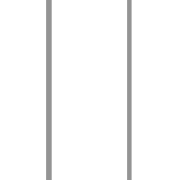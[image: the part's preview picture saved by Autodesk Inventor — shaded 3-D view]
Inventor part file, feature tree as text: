
AUTODESK INVENTOR PART (.ipt)
format: ipt  version: 2021 (Build 250183000, 183)  size: 129,536 bytes
history: native  units: in
note: dims shown in document units (in); Inventor stores cm internally (conversion verified against a paired STEP export)
features: other x4, sketch x4, plane x2, hole x1
ambient origin geometry x8: Origin, YZ Plane, XZ Plane, XY Plane, X Axis, Y Axis, Z Axis, Center Point
bodies: Solid1 (feature_tree), Body (feature_tree)
feature tree (11):
  other  "Driven Length"
  other  "Frame Generator"
  plane  "Work Plane3"
  other  "Start Plane"
  other  "End Plane"
  hole  "Hole2"  [1 undecoded]
  sketch  "Sketch"  dims[d4=2.0in d16=-0.0in d17=2.0in d18=0.12in d19=0.0in d22=1.5in d23=0.4375in d24=0.75in d25=0.635in d26=0.25in d27=0.5635in d28=1.0in d29=0.8108in d32=90.0deg d21=2.0in d8=0.5in d9=0.0344in d10=0.5in d11=0.0344in]
  sketch  "Sketch5"  dims[d0=1.5in d1=1.0in]
  sketch  "Sketch8"  dims[d2=0.0625in]
  plane  "Work Plane6"
  sketch  "Sketch9"  dims[d3=0.0625in]
note: 1 required parameter value undecoded (feature->parameter linkage not recoverable at this tier; creation-order binding heuristic only, values carry confidence <= 0.55)
